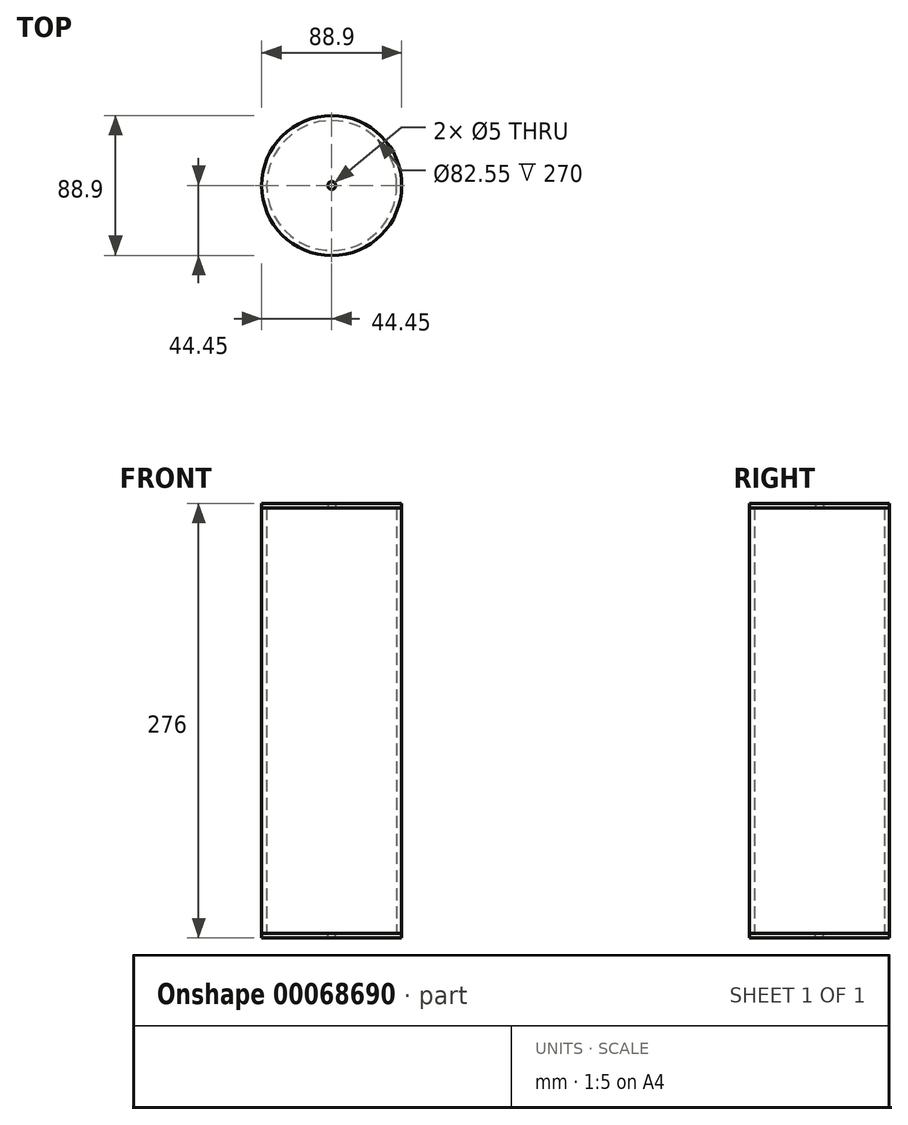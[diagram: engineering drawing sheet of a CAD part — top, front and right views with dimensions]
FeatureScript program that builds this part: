
annotation { "Feature Type Name" : "Feature", "Feature Type Description" : "" }
export const myFeature = defineFeature(function(context is Context, id is Id, definition is map)
    precondition{}
    {
        {
            assignVariable(context, id + "F0", {"name" : "SH", "anyValue" : 260});
        }
        {
            var Q0;
            Q0=qCreatedBy(makeId("Top.planeOp"),FACE);
            var sketch = newSketch(context, id + "F1", { "sketchPlane" : qUnion([Q0])});
            skCircle(sketch, "E0", {"center": v(0, 0) * mm, "radius": 41.28 * mm});
            skCircle(sketch, "E1", {"center": v(0, 0) * mm, "radius": 44.45 * mm});
            skSolve(sketch);
        }
        {
            var Q0;
            Q0 = qSketchRegion(id + "F1", true);
            extrude(context, id + "F2", {"entities" : qUnion([Q0]), "depth" : ((getVariable(context, 'SH')) * mm + 10 * mm) / 2, "hasSecondDirection" : true, "secondDirectionOppositeDirection" : true, "secondDirectionDepth" : ((getVariable(context, 'SH')) * mm + 10 * mm) / 2});
        }
        {
            var Q0;
            Q0=makeQuery(id+"F2.opExtrude","CAP_FACE",FACE,{"disambiguationData":[OSD([sQuery(id+"F1.wireOp",EDGE,"E0"),sQuery(id+"F1.wireOp",EDGE,"E1")])],"isStart":false});
            var sketch = newSketch(context, id + "F3", { "sketchPlane" : qUnion([Q0])});
            skCircle(sketch, "E2", {"center": v(0, 0) * mm, "radius": 44.45 * mm});
            skCircle(sketch, "E3", {"center": v(0, 0) * mm, "radius": 2.5 * mm});
            skSolve(sketch);
        }
        {
            var Q0;
            Q0 = qSketchRegion(id + "F3", true);
            extrude(context, id + "F4", {"entities" : qUnion([Q0]), "depth" : 3 * mm});
        }
        {
            var Q0;
            Q0=makeQuery(id+"F4.opExtrude","SWEPT_BODY",BODY,{"disambiguationData":[OSD([sQuery(id+"F3.wireOp",EDGE,"E2"),sQuery(id+"F3.wireOp",EDGE,"E3")])]});
            var Q1;
            Q1=qCreatedBy(makeId("Top.planeOp"),FACE);
            mirror(context, id + "F5", {"entities" : qUnion([Q0]), "mirrorPlane" : qUnion([Q1])});
        }
    });
